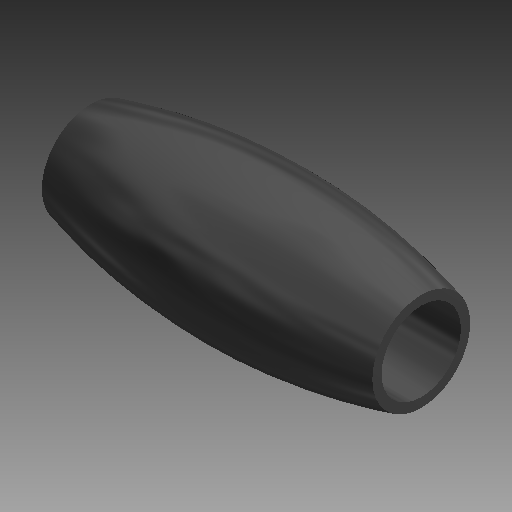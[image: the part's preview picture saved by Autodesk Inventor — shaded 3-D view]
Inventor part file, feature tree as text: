
AUTODESK INVENTOR PART (.ipt)
format: ipt  version: 2019 (Build 230136000, 136)  size: 102,912 bytes
history: native  units: mm (DEFAULTED — no unit token found)
features: revolve x1
ambient origin geometry x8: Origin, YZ Plane, XZ Plane, XY Plane, X Axis, Y Axis, Z Axis, Center Point
bodies: Solid1 (feature_tree)
feature tree (1):
  revolve  "Revolve1"  [1 undecoded]
note: 1 required parameter value undecoded (feature->parameter linkage not recoverable at this tier; creation-order binding heuristic only, values carry confidence <= 0.55)
